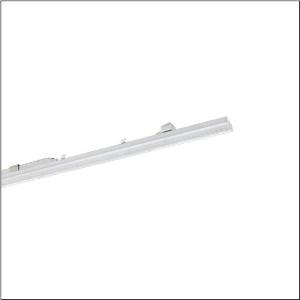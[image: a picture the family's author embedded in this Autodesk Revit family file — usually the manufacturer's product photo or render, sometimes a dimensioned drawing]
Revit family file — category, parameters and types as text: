
# Revit family: tl_l_5wd7a8f0b2c5
name_source: partatom
category: Lighting Fixtures
units: mm (PartAtom-declared; Revit-internal decimal feet)

## family parameters
Cut with Voids When Loaded = No
Host = Face
Light Source = No
Part Type = Normal
Room Calculation Point = No
Round Connector Dimension = Use Diameter
Shared = No

## types (1)
- TL L (1 x LED, 9800 lm, 63.3 W, 4000K)
    Apparent Load = 63 VA
    CIE Flux Codes = 49 84 98 100 100
    Color Rendering = 80
    Color Temperature = 4000K
    Default Elevation = 1800 mm
    Description = TL L, luminaire insert, of sheet steel, galvanised, coil coated, white, length: 1.500mm, width: 66mm, height: 67mm, micro fuse,LED rated luminous flux: 9.800lm, light colour: 840, control gear: 4..20mA, with terminal, 5-pole, mains connection: 230..240V, AC, 50/60Hz, rated input power: 63W, primary optical cover: cover, of PMMA, light emission: direct distribution, protection rating (complete): as luminaire, insulation class (complete): insulation class I (protective earthing), certification: CE, impact resistance: IK06, permissible ambient temperature for indoor applications: -25..+35°C, packaging unit: 1 piece
    Height = 120 mm
    Lamp = 1 x LED
    Lamp Light Flux = 9800 lm
    Lamp Power = 63.3 W
    Lamp count = 1
    Length = 1690 mm
    Luminous efficacy = 155 lm/W
    Manufacturer = Siteco
    ModVariant = No
    Model = 5WD7A8F0B2C5
    Mounting Place = Ceiling
    Mounting Type = Pendant
    Number of Poles = 1
    OnlyDefault = Yes
    Power Factor = 1
    Product Name = TL L
    Product group = luminaire insert
    ProductGroupID = 901
    Protection Class = Protection class I
    Protection Degree = Degree of protection
    RLX_Detail_Level = 1
    RLX_Emergency_Light_Flux = 0 lm
    RLX_Emergency_Type = 0
    RLX_Emergency_Type_DB = No
    RlxData = <blob elided: 14133 chars, md5=0c2fcd9c>
    Socket = socket
    Standby Power = 0 W
    System Light Flux = 9800 lm
    System Power = 63 W
    Type Comments = Product without accessories
    Type Image = l_1294382.jpg
    URL = http://relux.com
    VarID = ---
    Voltage = 0 V
    Weight = 0.00 kg
    Width = 208 mm

## geometry (parser evidence)
native form markers: Sweep x12
no freeform markers — native parametric forms only
